# Revit family: HL_Электронный модуль управления_HL0710E.0EPC_Low_Voltage.rfa
name_source: partatom
category: Elektrická tělesa
revit_build: Autodesk Revit 2016 (Build: 20161004_0715(x64)
units: mm (PartAtom-declared; Revit-internal decimal feet)

## family parameters
Bod výpočtu místnosti = Ne
Kóta kulaté spojky = Použít průměr
Nadpis OmniClass = Environmental Controls
Ořezat dutým tvarem při načtení = Ne
Sdílené = Ano
Typ součásti = Normální
Vždy vertikální = Ano
Zachovat orientaci poznámky = Ne
Založené na pracovní rovině = Ne
Číslo OmniClass = 23.85.80.11.24

## types (1)
- HL_Электронный модуль управления_HL0710E.0EPC_Low_Voltage.rfa
    Cena = 0 $
    EAN = 9003076009800
    Klíčová poznámka = HL0710E.0EPC
    Komentáře k typům = Электронный модул с возможностью подключения
    Model = HL0710E.0EPC
    Popis = Механический канализационный затвор
    URL = http://www.hutterer-lechner.com
    Výrobce = HL Hutterer & Lechner GmbH
    ВЕС = 1,357 kg
    Классификация нагрузок = 1
    Количество полюсов = 1
    Коэффициент мощности = Other
    Напряжение = 230 V
    полная установленная мощность фаза = 0 VA
